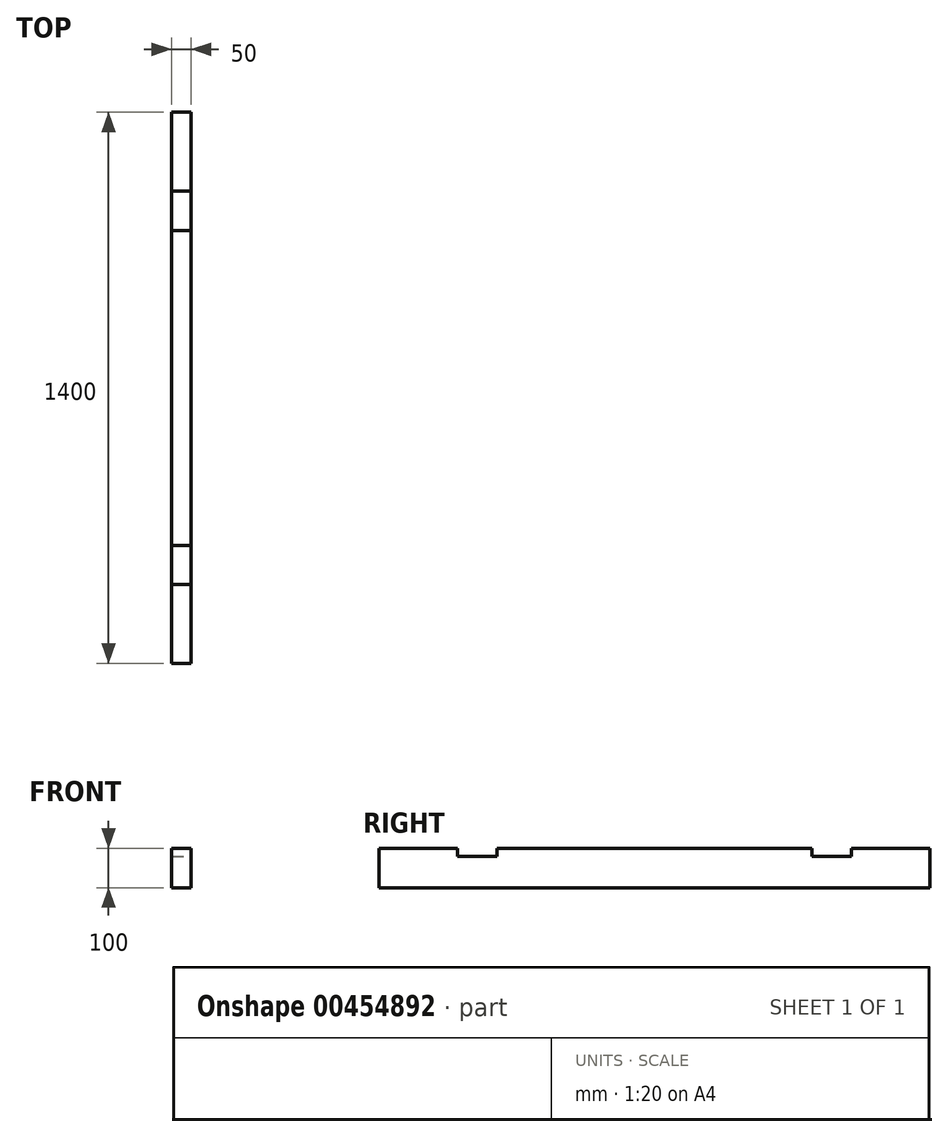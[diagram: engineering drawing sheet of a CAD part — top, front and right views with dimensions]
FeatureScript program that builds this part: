
annotation { "Feature Type Name" : "Feature", "Feature Type Description" : "" }
export const myFeature = defineFeature(function(context is Context, id is Id, definition is map)
    precondition{}
    {
        {
            var Q0;
            Q0=qCreatedBy(makeId("Front.planeOp"),FACE);
            var sketch = newSketch(context, id + "F0", { "sketchPlane" : qUnion([Q0])});
            skLineSegment(sketch, "E0.bottom", {"start": v(0, 0) * mm, "end": v(50, 0) * mm});
            skLineSegment(sketch, "E0.top", {"start": v(0, 100) * mm, "end": v(50, 100) * mm});
            skLineSegment(sketch, "E0.left", {"start": v(0, 0) * mm, "end": v(0, 100) * mm});
            skLineSegment(sketch, "E0.right", {"start": v(50, 0) * mm, "end": v(50, 100) * mm});
            skSolve(sketch);
        }
        {
            var Q0;
            Q0 = qSketchRegion(id + "F0", true);
            extrude(context, id + "F1", {"entities" : qUnion([Q0]), "depth" : 1400 * mm});
        }
        {
            var Q0;
            Q0=makeQuery(id+"F1.opExtrude","SWEPT_FACE",FACE,{"disambiguationData":[OSD([sQuery(id+"F0.wireOp",EDGE,"E0.right")])]});
            var sketch = newSketch(context, id + "F2", { "sketchPlane" : qUnion([Q0])});
            skLineSegment(sketch, "E1.bottom", {"start": v(-200, 100) * mm, "end": v(-300, 100) * mm});
            skLineSegment(sketch, "E1.top", {"start": v(-200, 80) * mm, "end": v(-300, 80) * mm});
            skLineSegment(sketch, "E1.left", {"start": v(-200, 100) * mm, "end": v(-200, 80) * mm});
            skLineSegment(sketch, "E1.right", {"start": v(-300, 100) * mm, "end": v(-300, 80) * mm});
            skLineSegment(sketch, "E2.bottom", {"start": v(-1200, 100) * mm, "end": v(-1100, 100) * mm});
            skLineSegment(sketch, "E2.top", {"start": v(-1200, 80) * mm, "end": v(-1100, 80) * mm});
            skLineSegment(sketch, "E2.left", {"start": v(-1200, 100) * mm, "end": v(-1200, 80) * mm});
            skLineSegment(sketch, "E2.right", {"start": v(-1100, 100) * mm, "end": v(-1100, 80) * mm});
            skSolve(sketch);
        }
        {
            var Q0;
            Q0 = qSketchRegion(id + "F2", true);
            extrude(context, id + "F3", {"entities" : qUnion([Q0]), "operationType" : NewBodyOperationType.REMOVE, "endBound" : BoundingType.THROUGH_ALL, "oppositeDirection" : true, "depth" : 25.4 * mm});
        }
    });
